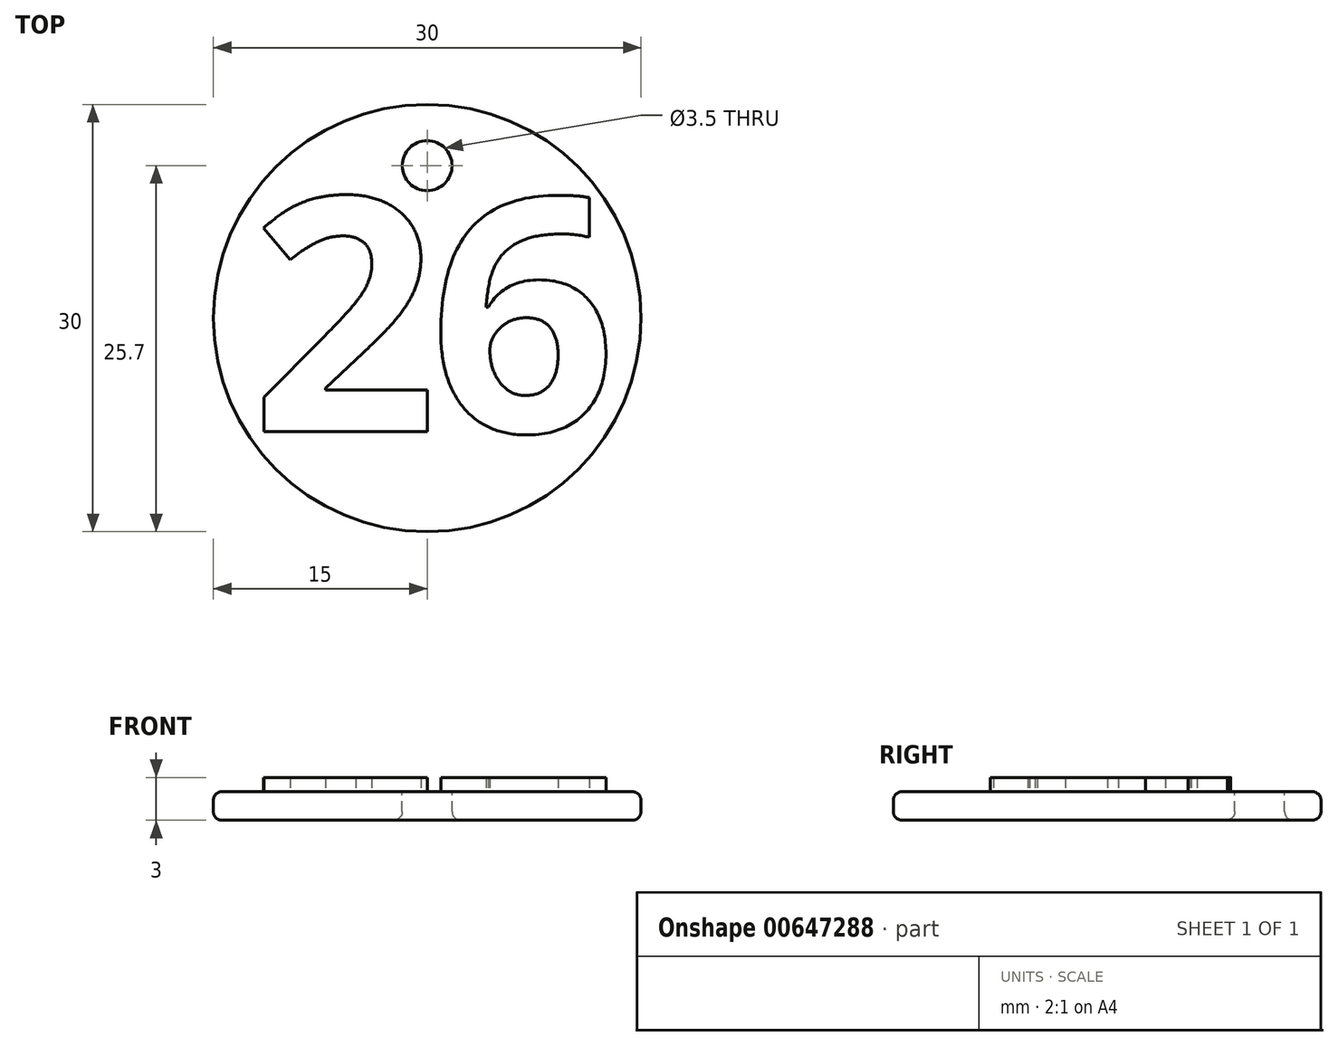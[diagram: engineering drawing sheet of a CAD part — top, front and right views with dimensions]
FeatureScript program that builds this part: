
annotation { "Feature Type Name" : "Feature", "Feature Type Description" : "" }
export const myFeature = defineFeature(function(context is Context, id is Id, definition is map)
    precondition{}
    {
        {
            var Q0;
            Q0=qCreatedBy(makeId("Top.planeOp"),FACE);
            var sketch = newSketch(context, id + "F0", { "sketchPlane" : qUnion([Q0])});
            skCircle(sketch, "E0", {"center": v(0, 0) * mm, "radius": 15 * mm});
            skSolve(sketch);
        }
        {
            var Q0;
            Q0=makeQuery(id+"F0.imprint","IMPRINT",FACE,{"disambiguationData":[TD([[makeQuery(id+"F0.imprint","IMPRINT",EDGE,{"derivedFrom":sQuery(id+"F0.wireOp",EDGE,"E0")}),1.0]])]});
            extrude(context, id + "F1", {"entities" : qUnion([Q0]), "depth" : 2 * mm, "offsetDistance" : 25 * mm});
        }
        {
            var Q0;
            {var subQ0=sQuery(id+"F0.wireOp",EDGE,"E0");Q0=makeQuery(id+"F4hHrE028sntqlZ_1.boolean.opBoolean","SPLIT",FACE,{"disambiguationData":[TD([makeQuery(id+"F1.opExtrude","SWEPT_FACE",FACE,{"disambiguationData":[OSD([subQ0])]})])],"derivedFrom":makeQuery(id+"F1.opExtrude","CAP_FACE",FACE,{"disambiguationData":[OSD([subQ0])],"isStart":false})});}
            var sketch = newSketch(context, id + "F2", { "sketchPlane" : qUnion([Q0])});
            skCircle(sketch, "E1", {"center": v(0, 10.7) * mm, "radius": 1.75 * mm});
            skSolve(sketch);
        }
        {
            var Q0;
            Q0=makeQuery(id+"F2.imprint","IMPRINT",FACE,{"disambiguationData":[TD([[makeQuery(id+"F2.imprint","IMPRINT",EDGE,{"derivedFrom":sQuery(id+"F2.wireOp",EDGE,"E1")}),1.0]])]});
            extrude(context, id + "F3", {"entities" : qUnion([Q0]), "operationType" : NewBodyOperationType.REMOVE, "endBound" : BoundingType.THROUGH_ALL, "oppositeDirection" : true, "depth" : 25 * mm, "offsetDistance" : 25 * mm});
        }
        {
            var Q0;
            Q0=makeQuery(id+"F1.opExtrude","CAP_EDGE",EDGE,{"disambiguationData":[OSD([sQuery(id+"F0.wireOp",EDGE,"E0")])],"isStart":false});
            var Q1;
            Q1=makeQuery(id+"F3.boolean.opBoolean","COPY",EDGE,{"derivedFrom":makeQuery(id+"F3.opExtrude","CAP_EDGE",EDGE,{"disambiguationData":[OSD([sQuery(id+"F2.wireOp",EDGE,"E1")])],"isStart":true})});
            var Q2;
            Q2=makeQuery(id+"F3.boolean.opBoolean","INTERSECT",EDGE,{"derivedFrom":[makeQuery(id+"F1.opExtrude","CAP_FACE",FACE,{"disambiguationData":[OSD([sQuery(id+"F0.wireOp",EDGE,"E0")])],"isStart":true}),makeQuery(id+"F3.opExtrude","SWEPT_FACE",FACE,{"disambiguationData":[OSD([sQuery(id+"F2.wireOp",EDGE,"E1")])]})]});
            var Q3;
            Q3=makeQuery(id+"F1.opExtrude","CAP_EDGE",EDGE,{"disambiguationData":[OSD([sQuery(id+"F0.wireOp",EDGE,"E0")])],"isStart":true});
            fillet(context, id + "F4", {"entities" : qUnion([Q0, Q1, Q2, Q3]), "radius" : 0.6 * mm, "tangentPropagation" : true, "allowEdgeOverflow" : false});
        }
        {
            var Q0;
            Q0=makeQuery(id+"F1.opExtrude","CAP_FACE",FACE,{"disambiguationData":[OSD([sQuery(id+"F0.wireOp",EDGE,"E0")])],"isStart":false});
            var sketch = newSketch(context, id + "F5", { "sketchPlane" : qUnion([Q0])});
            skText(sketch, "E2", { "text": "2", "fontName": "OpenSans-Bold.ttf"});
            skText(sketch, "E3", { "text": "6", "fontName": "OpenSans-Bold.ttf"});
            const initialGuessF5  = {"E2": [-0.01237, -0.00798, 1, 0, 0.01655], "E3": [0.00015, -0.00798, 1, 0, 0.01655]};
            skSetInitialGuess(sketch, initialGuessF5);
            skSolve(sketch);
        }
        {
            var Q0;
            Q0 = qSketchRegion(id + "F5", true);
            extrude(context, id + "F6", {"entities" : qUnion([Q0]), "operationType" : NewBodyOperationType.ADD, "depth" : 1 * mm, "offsetDistance" : 25 * mm});
        }
    });
